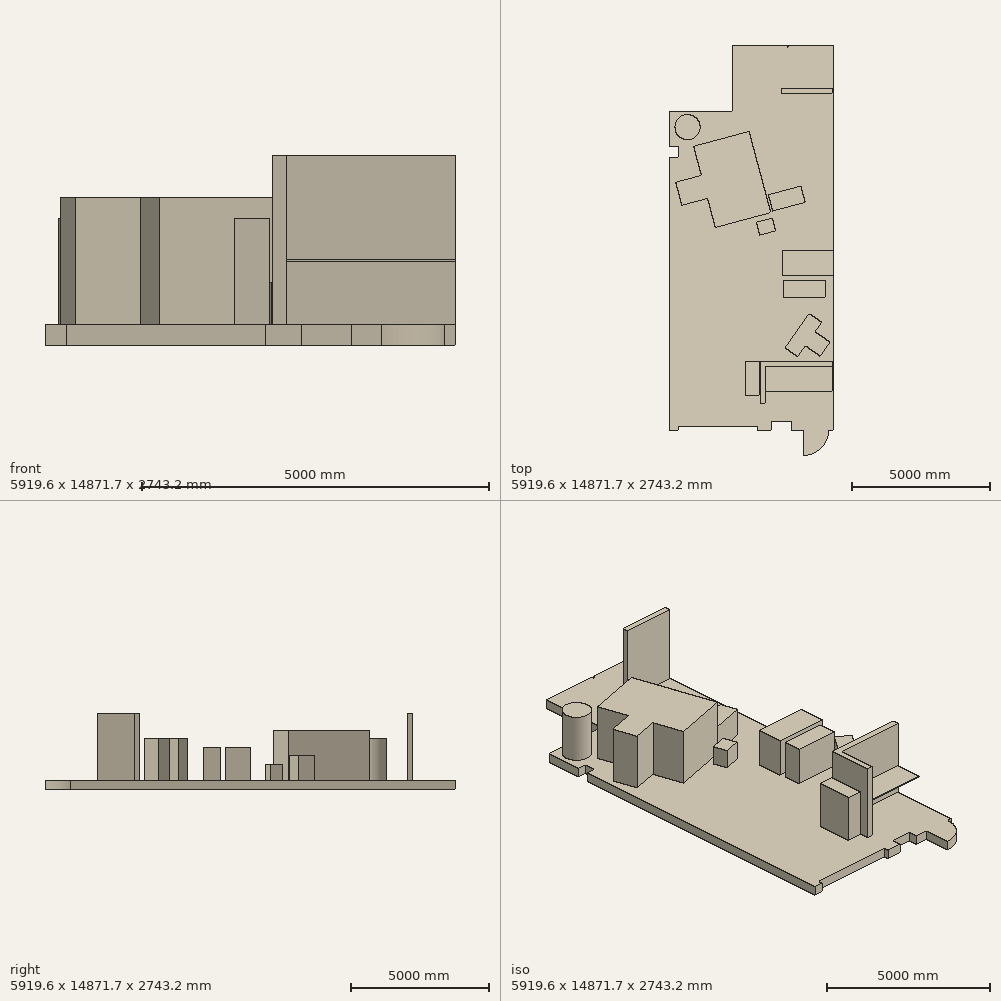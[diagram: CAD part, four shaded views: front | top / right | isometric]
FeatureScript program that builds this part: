
annotation { "Feature Type Name" : "Feature", "Feature Type Description" : "" }
export const myFeature = defineFeature(function(context is Context, id is Id, definition is map)
    precondition{}
    {
        {
            var Q0;
            Q0=qCreatedBy(makeId("Top.planeOp"),FACE);
            var sketch = newSketch(context, id + "F0", { "sketchPlane" : qUnion([Q0])});
            skLineSegment(sketch, "E0.bottom", {"start": v(-758.75, 6768.86) * mm, "end": v(2873.45, 6768.86) * mm});
            skLineSegment(sketch, "E0.top", {"start": v(-3044.75, -7188.44) * mm, "end": v(-2739.95, -7188.44) * mm});
            skLineSegment(sketch, "E0.left", {"start": v(-3044.75, 4368.56) * mm, "end": v(-3044.75, -7188.44) * mm});
            skLineSegment(sketch, "E0.right", {"start": v(2873.45, 6768.86) * mm, "end": v(2873.45, -7188.44) * mm});
            skPoint(sketch, "E0.middle", {"position": v(-85.65, -209.8) * mm});
            skLineSegment(sketch, "E1", {"start": v(-3044.75, 4368.56) * mm, "end": v(-758.75, 4368.56) * mm});
            skLineSegment(sketch, "E2", {"start": v(-758.75, 6768.86) * mm, "end": v(-758.75, 4368.56) * mm});
            skPoint(sketch, "E3.orphan", {"position": v(-3044.75, 6768.86) * mm});
            skLineSegment(sketch, "E4.top", {"start": v(-2739.95, -7036.04) * mm, "end": v(130.25, -7036.04) * mm});
            skLineSegment(sketch, "E4.left", {"start": v(-2739.95, -7188.44) * mm, "end": v(-2739.95, -7036.04) * mm});
            skLineSegment(sketch, "E4.right", {"start": v(130.25, -7188.44) * mm, "end": v(130.25, -7036.04) * mm});
            skLineSegment(sketch, "E5", {"start": v(1806.65, -7188.44) * mm, "end": v(1806.65, -8102.84) * mm});
            skPoint(sketch, "E6", {"position": v(2721.05, -7188.44) * mm});
            skArc(sketch, "E7", {"start": v(2721.05, -7188.44) * mm, "mid": v(2453.23, -7835.02) * mm, "end": v(1806.65, -8102.84) * mm});
            skLineSegment(sketch, "E8.trimOffspring", {"start": v(2721.05, -7188.44) * mm, "end": v(2873.45, -7188.44) * mm});
            skLineSegment(sketch, "E9.trimOffspring", {"start": v(130.25, -7188.44) * mm, "end": v(1806.65, -7188.44) * mm});
            skLineSegment(sketch, "E10.bottom", {"start": v(650.95, -7188.44) * mm, "end": v(1374.85, -7188.44) * mm});
            skLineSegment(sketch, "E10.top", {"start": v(650.95, -6883.64) * mm, "end": v(1374.85, -6883.64) * mm});
            skLineSegment(sketch, "E10.left", {"start": v(650.95, -7188.44) * mm, "end": v(650.95, -6883.64) * mm});
            skLineSegment(sketch, "E10.right", {"start": v(1374.85, -7188.44) * mm, "end": v(1374.85, -6883.64) * mm});
            skLineSegment(sketch, "E11.bottom", {"start": v(1222.45, 6768.86) * mm, "end": v(1273.25, 6768.86) * mm});
            skLineSegment(sketch, "E11.top", {"start": v(1222.45, 6679.15) * mm, "end": v(1273.25, 6679.15) * mm});
            skLineSegment(sketch, "E11.left", {"start": v(1273.25, 6768.86) * mm, "end": v(1273.25, 6679.15) * mm});
            skLineSegment(sketch, "E11.right", {"start": v(1222.45, 6768.86) * mm, "end": v(1222.45, 6679.15) * mm});
            skLineSegment(sketch, "E12.bottom", {"start": v(-3044.75, 3098.56) * mm, "end": v(-2739.95, 3098.56) * mm});
            skLineSegment(sketch, "E12.top", {"start": v(-3044.75, 2704.86) * mm, "end": v(-2739.95, 2704.86) * mm});
            skLineSegment(sketch, "E12.left", {"start": v(-3044.75, 3098.56) * mm, "end": v(-3044.75, 2704.86) * mm});
            skLineSegment(sketch, "E12.right", {"start": v(-2739.95, 3098.56) * mm, "end": v(-2739.95, 2704.86) * mm});
            skSolve(sketch);
        }
        {
            var Q0;
            Q0=qCreatedBy(makeId("Top.planeOp"),FACE);
            var sketch = newSketch(context, id + "F1", { "sketchPlane" : qUnion([Q0])});
            skPoint(sketch, "E13", {"position": v(-269.7, 6243.01) * mm});
            skCircle(sketch, "E14", {"center": v(-269.7, 6243.01) * mm, "radius": 457.2 * mm});
            skLineSegment(sketch, "E15.bottom", {"start": v(-2184.07, 3463.75) * mm, "end": v(-172.24, 4002.82) * mm});
            skLineSegment(sketch, "E15.top", {"start": v(-1395.19, 519.6) * mm, "end": v(616.64, 1058.68) * mm});
            skLineSegment(sketch, "E15.left", {"start": v(-2833.7, 2158.95) * mm, "end": v(-2610.18, 1324.78) * mm});
            skLineSegment(sketch, "E15.right", {"start": v(-172.24, 4002.82) * mm, "end": v(616.64, 1058.68) * mm});
            skPoint(sketch, "E15.middle", {"position": v(-777.7, 2217.11) * mm});
            skLineSegment(sketch, "E16.bottom", {"start": v(669.24, 862.4) * mm, "end": v(89.62, 707.1) * mm});
            skLineSegment(sketch, "E16.top", {"start": v(794.14, 396.25) * mm, "end": v(214.53, 240.94) * mm});
            skLineSegment(sketch, "E16.left", {"start": v(669.24, 862.4) * mm, "end": v(794.14, 396.25) * mm});
            skLineSegment(sketch, "E16.right", {"start": v(89.62, 707.1) * mm, "end": v(214.53, 240.94) * mm});
            skLineSegment(sketch, "E17.bottom", {"start": v(2549.7, 6752.11) * mm, "end": v(2041.7, 6752.11) * mm});
            skLineSegment(sketch, "E17.top", {"start": v(2549.7, 6142.51) * mm, "end": v(2041.7, 6142.51) * mm});
            skLineSegment(sketch, "E17.left", {"start": v(2549.7, 6752.11) * mm, "end": v(2549.7, 6142.51) * mm});
            skLineSegment(sketch, "E17.right", {"start": v(2041.7, 6752.11) * mm, "end": v(2041.7, 6142.51) * mm});
            skLineSegment(sketch, "E18.bottom", {"start": v(924.1, 6752.11) * mm, "end": v(1533.7, 6752.11) * mm});
            skLineSegment(sketch, "E18.top", {"start": v(924.1, 6330.69) * mm, "end": v(1533.7, 6330.69) * mm});
            skLineSegment(sketch, "E18.left", {"start": v(924.1, 6752.11) * mm, "end": v(924.1, 6330.69) * mm});
            skLineSegment(sketch, "E18.right", {"start": v(1533.7, 6752.11) * mm, "end": v(1533.7, 6330.69) * mm});
            skLineSegment(sketch, "E19.bottom", {"start": v(2846.22, 5215.41) * mm, "end": v(1017.42, 5215.41) * mm});
            skLineSegment(sketch, "E19.top", {"start": v(2846.22, 5012.21) * mm, "end": v(1017.42, 5012.21) * mm});
            skLineSegment(sketch, "E19.left", {"start": v(2846.22, 5215.41) * mm, "end": v(2846.22, 5012.21) * mm});
            skLineSegment(sketch, "E19.right", {"start": v(1017.42, 5215.41) * mm, "end": v(1017.42, 5012.21) * mm});
            skLineSegment(sketch, "E20.bottom", {"start": v(527.51, 1655.28) * mm, "end": v(1705.17, 1970.83) * mm});
            skLineSegment(sketch, "E20.top", {"start": v(685.29, 1066.45) * mm, "end": v(1862.94, 1382) * mm});
            skLineSegment(sketch, "E20.left", {"start": v(527.51, 1655.28) * mm, "end": v(685.29, 1066.45) * mm});
            skLineSegment(sketch, "E20.right", {"start": v(1705.17, 1970.83) * mm, "end": v(1862.94, 1382) * mm});
            skLineSegment(sketch, "E21.bottom", {"start": v(228.15, -6200.2) * mm, "end": v(431.35, -6200.2) * mm});
            skLineSegment(sketch, "E21.top", {"start": v(228.15, -4676.2) * mm, "end": v(431.35, -4676.2) * mm});
            skLineSegment(sketch, "E21.left", {"start": v(228.15, -6200.2) * mm, "end": v(228.15, -4676.2) * mm});
            skLineSegment(sketch, "E21.right", {"start": v(431.35, -6200.2) * mm, "end": v(431.35, -4879.4) * mm});
            skLineSegment(sketch, "E22", {"start": v(431.35, -4676.2) * mm, "end": v(2869.75, -4676.2) * mm});
            skLineSegment(sketch, "E23", {"start": v(2869.75, -4676.2) * mm, "end": v(2869.75, -4879.4) * mm});
            skLineSegment(sketch, "E24", {"start": v(2869.75, -4879.4) * mm, "end": v(431.35, -4879.4) * mm});
            skPoint(sketch, "E25", {"position": v(1430.43, -5379.79) * mm});
            skLineSegment(sketch, "E26.bottom", {"start": v(-314.55, -5910.65) * mm, "end": v(-314.55, -4691.45) * mm});
            skLineSegment(sketch, "E26.top", {"start": v(193.45, -5910.65) * mm, "end": v(193.45, -4691.45) * mm});
            skLineSegment(sketch, "E26.left", {"start": v(-314.55, -5910.65) * mm, "end": v(193.45, -5910.65) * mm});
            skLineSegment(sketch, "E26.right", {"start": v(-314.55, -4691.45) * mm, "end": v(193.45, -4691.45) * mm});
            skPoint(sketch, "E26.middle", {"position": v(1090.07, -4417.13) * mm});
            skLineSegment(sketch, "E27.bottom", {"start": v(2874.83, -1686.87) * mm, "end": v(1046.03, -1686.87) * mm});
            skLineSegment(sketch, "E27.top", {"start": v(2874.83, -772.47) * mm, "end": v(1046.03, -772.47) * mm});
            skLineSegment(sketch, "E27.left", {"start": v(2874.83, -1686.87) * mm, "end": v(2874.83, -772.47) * mm});
            skLineSegment(sketch, "E27.right", {"start": v(1046.03, -1686.87) * mm, "end": v(1046.03, -772.47) * mm});
            skPoint(sketch, "E27.middle", {"position": v(-1844.5, -983.29) * mm});
            skLineSegment(sketch, "E28.bottom", {"start": v(-432.25, -2672.14) * mm, "end": v(177.35, -2672.14) * mm});
            skLineSegment(sketch, "E28.top", {"start": v(-432.25, -4196.14) * mm, "end": v(177.35, -4196.14) * mm});
            skLineSegment(sketch, "E28.left", {"start": v(-432.25, -2672.14) * mm, "end": v(-432.25, -4196.14) * mm});
            skLineSegment(sketch, "E28.right", {"start": v(177.35, -2672.14) * mm, "end": v(177.35, -4196.14) * mm});
            skPoint(sketch, "E28.middle", {"position": v(-2606.5, -2479.1) * mm});
            skLineSegment(sketch, "E29.bottom", {"start": v(2012.55, -2954.44) * mm, "end": v(2469.79, -3274.6) * mm});
            skLineSegment(sketch, "E29.top", {"start": v(1138.42, -4202.83) * mm, "end": v(1595.66, -4523) * mm});
            skLineSegment(sketch, "E29.left", {"start": v(2012.55, -2954.44) * mm, "end": v(1138.42, -4202.83) * mm});
            skLineSegment(sketch, "E29.right", {"start": v(2770.78, -3997.2) * mm, "end": v(2414.24, -4506.38) * mm});
            skPoint(sketch, "E29.middle", {"position": v(-168.1, -2475.87) * mm});
            skLineSegment(sketch, "E30", {"start": v(-2833.7, 2158.95) * mm, "end": v(-1901.38, 2408.77) * mm});
            skLineSegment(sketch, "E31", {"start": v(-2610.18, 1324.78) * mm, "end": v(-1677.87, 1574.6) * mm});
            skLineSegment(sketch, "E32", {"start": v(-2184.07, 3463.75) * mm, "end": v(-1901.38, 2408.77) * mm});
            skLineSegment(sketch, "E33", {"start": v(-1395.19, 519.6) * mm, "end": v(-1677.87, 1574.6) * mm});
            skPoint(sketch, "E34.orphan", {"position": v(-2301.7, 3741.11) * mm});
            skPoint(sketch, "E35.orphan", {"position": v(-2301.7, 693.11) * mm});
            skLineSegment(sketch, "E36.0", {"start": v(669.24, 862.4) * mm, "end": v(616.64, 1058.68) * mm, "construction": true});
            skLineSegment(sketch, "E37", {"start": v(2770.78, -3997.2) * mm, "end": v(2229.3, -3618.05) * mm});
            skLineSegment(sketch, "E38", {"start": v(2229.3, -3618.05) * mm, "end": v(2469.79, -3274.6) * mm});
            skLineSegment(sketch, "E39", {"start": v(2414.24, -4506.38) * mm, "end": v(1872.77, -4127.24) * mm});
            skLineSegment(sketch, "E40", {"start": v(1872.77, -4127.24) * mm, "end": v(1595.66, -4523) * mm});
            skPoint(sketch, "E41.orphan", {"position": v(441.5, -1713.87) * mm});
            skPoint(sketch, "E42.orphan", {"position": v(441.5, -3237.87) * mm});
            skLineSegment(sketch, "E43.0", {"start": v(1872.77, -4127.24) * mm, "end": v(2229.3, -3618.05) * mm, "construction": true});
            skSolve(sketch);
        }
        {
            var Q0;
            Q0=makeQuery(id+"F1.imprint","IMPRINT",FACE,{"disambiguationData":[TD([[makeQuery(id+"F1.imprint","IMPRINT",EDGE,{"derivedFrom":sQuery(id+"F1.wireOp",EDGE,"E15.bottom")}),-1.0]])]});
            extrude(context, id + "F2", {"entities" : qUnion([Q0]), "depth" : 1828.8 * mm});
        }
        {
            var Q0;
            Q0=makeQuery(id+"F1.imprint","IMPRINT",FACE,{"disambiguationData":[TD([[makeQuery(id+"F1.imprint","IMPRINT",EDGE,{"derivedFrom":sQuery(id+"F1.wireOp",EDGE,"E20.bottom")}),-1.0]])]});
            extrude(context, id + "F3", {"entities" : qUnion([Q0]), "depth" : 914.4 * mm});
        }
        {
            var Q0;
            Q0=makeQuery(id+"F1.imprint","IMPRINT",FACE,{"disambiguationData":[TD([[makeQuery(id+"F1.imprint","IMPRINT",EDGE,{"derivedFrom":sQuery(id+"F1.wireOp",EDGE,"E16.bottom")}),1.0]])]});
            extrude(context, id + "F4", {"entities" : qUnion([Q0]), "depth" : 609.6 * mm});
        }
        {
            var Q0;
            Q0=makeQuery(id+"F1.imprint","IMPRINT",FACE,{"disambiguationData":[TD([[makeQuery(id+"F1.imprint","IMPRINT",EDGE,{"derivedFrom":sQuery(id+"F1.wireOp",EDGE,"E27.bottom")}),-1.0]])]});
            extrude(context, id + "F5", {"entities" : qUnion([Q0]), "depth" : 1219.2 * mm});
        }
        {
            var Q0;
            Q0=makeQuery(id+"F1.imprint","IMPRINT",FACE,{"disambiguationData":[TD([[makeQuery(id+"F1.imprint","IMPRINT",EDGE,{"derivedFrom":sQuery(id+"F1.wireOp",EDGE,"E28.bottom")}),-1.0]])]});
            extrude(context, id + "F6", {"entities" : qUnion([Q0]), "depth" : 1219.2 * mm});
        }
        {
            var Q0;
            Q0=makeQuery(id+"F1.imprint","IMPRINT",FACE,{"disambiguationData":[TD([[makeQuery(id+"F1.imprint","IMPRINT",EDGE,{"derivedFrom":sQuery(id+"F1.wireOp",EDGE,"E29.bottom")}),-1.0]])]});
            extrude(context, id + "F7", {"entities" : qUnion([Q0]), "depth" : 1524 * mm});
        }
        {
            var Q0;
            Q0=makeQuery(id+"F1.imprint","IMPRINT",FACE,{"disambiguationData":[TD([[makeQuery(id+"F1.imprint","IMPRINT",EDGE,{"derivedFrom":sQuery(id+"F1.wireOp",EDGE,"E14")}),1.0]])]});
            var Q1;
            Q1=makeQuery(id+"F1.imprint","IMPRINT",FACE,{"disambiguationData":[TD([[makeQuery(id+"F1.imprint","IMPRINT",EDGE,{"derivedFrom":sQuery(id+"F1.wireOp",EDGE,"E26.bottom")}),-1.0]])]});
            var Q2;
            Q2=sQuery(id+"F1.wireOp",EDGE,"E14");
            var Q3;
            Q3=sQuery(id+"F1.wireOp",EDGE,"E26.right");
            var Q4;
            Q4=sQuery(id+"F1.wireOp",EDGE,"E26.bottom");
            var Q5;
            Q5=sQuery(id+"F1.wireOp",EDGE,"E26.top");
            var Q6;
            Q6=sQuery(id+"F1.wireOp",EDGE,"E26.left");
            extrude(context, id + "F8", {"entities" : qUnion([Q0, Q1]), "operationType" : NewBodyOperationType.ADD, "surfaceEntities" : qUnion([Q2, Q3, Q4, Q5, Q6]), "depth" : 1524 * mm});
        }
        {
            var Q0;
            Q0=makeQuery(id+"F1.imprint","IMPRINT",FACE,{"disambiguationData":[TD([[makeQuery(id+"F1.imprint","IMPRINT",EDGE,{"derivedFrom":sQuery(id+"F1.wireOp",EDGE,"E21.bottom")}),1.0]])]});
            extrude(context, id + "F9", {"entities" : qUnion([Q0]), "depth" : 2438.4 * mm});
        }
        {
            var Q0;
            Q0=makeQuery(id+"F1.imprint","IMPRINT",FACE,{"disambiguationData":[TD([[makeQuery(id+"F1.imprint","IMPRINT",EDGE,{"derivedFrom":sQuery(id+"F1.wireOp",EDGE,"E19.bottom")}),1.0]])]});
            extrude(context, id + "F10", {"entities" : qUnion([Q0]), "depth" : 2438.4 * mm});
        }
        {
            var Q0;
            {var subQ12=sQuery(id+"F0.wireOp",EDGE,"E0.top");Q0=makeQuery(id+"F0.imprint","IMPRINT",FACE,{"disambiguationData":[TD([[makeQuery(id+"F0.imprint","IMPRINT",EDGE,{"derivedFrom":subQ12}),1.0]])]});}
            extrude(context, id + "F11", {"entities" : qUnion([Q0]), "oppositeDirection" : true, "depth" : 304.8 * mm});
        }
        {
            var Q0;
            Q0=makeQuery(id+"F9.opExtrude","SWEPT_FACE",FACE,{"disambiguationData":[OSD([sQuery(id+"F1.wireOp",EDGE,"E24")])]});
            var sketch = newSketch(context, id + "F12", { "sketchPlane" : qUnion([Q0])});
            skLineSegment(sketch, "E44.bottom", {"start": v(431.35, 914.4) * mm, "end": v(2869.75, 914.4) * mm});
            skLineSegment(sketch, "E44.top", {"start": v(431.35, 939.8) * mm, "end": v(2869.75, 939.8) * mm});
            skLineSegment(sketch, "E44.left", {"start": v(431.35, 939.8) * mm, "end": v(431.35, 914.4) * mm});
            skLineSegment(sketch, "E44.right", {"start": v(2869.75, 939.8) * mm, "end": v(2869.75, 914.4) * mm});
            skSolve(sketch);
        }
        {
            var Q0;
            Q0 = qSketchRegion(id + "F12", true);
            extrude(context, id + "F13", {"entities" : qUnion([Q0]), "operationType" : NewBodyOperationType.ADD, "depth" : 914.4 * mm});
        }
        {
            var Q0;
            Q0=makeQuery(id+"F2.opExtrude","SWEPT_BODY",BODY,{"disambiguationData":[OSD([sQuery(id+"F1.wireOp",EDGE,"E15.bottom"),sQuery(id+"F1.wireOp",EDGE,"E15.top"),sQuery(id+"F1.wireOp",EDGE,"E15.left"),sQuery(id+"F1.wireOp",EDGE,"E15.right"),sQuery(id+"F1.wireOp",EDGE,"E30"),sQuery(id+"F1.wireOp",EDGE,"E31"),sQuery(id+"F1.wireOp",EDGE,"E32"),sQuery(id+"F1.wireOp",EDGE,"E33")])]});
            transform(context, id + "F14", {"entities" : qUnion([Q0]), "transformType" : TransformType.TRANSLATION_3D, "dx" : 0 * mm, "dy" : -914.4 * mm, "dz" : 0 * mm, "makeCopy" : false});
        }
        {
            var Q0;
            Q0=makeQuery(id+"F5.opExtrude","SWEPT_BODY",BODY,{"disambiguationData":[OSD([sQuery(id+"F1.wireOp",EDGE,"E27.bottom"),sQuery(id+"F1.wireOp",EDGE,"E27.top"),sQuery(id+"F1.wireOp",EDGE,"E27.left"),sQuery(id+"F1.wireOp",EDGE,"E27.right")])]});
            transform(context, id + "F15", {"entities" : qUnion([Q0]), "transformType" : TransformType.TRANSLATION_3D, "dx" : 0 * mm, "dy" : -609.6 * mm, "dz" : 0 * mm, "makeCopy" : false});
        }
        {
            var Q0;
            Q0=makeQuery(id+"F4.opExtrude","SWEPT_BODY",BODY,{"disambiguationData":[OSD([sQuery(id+"F1.wireOp",EDGE,"E16.bottom"),sQuery(id+"F1.wireOp",EDGE,"E16.top"),sQuery(id+"F1.wireOp",EDGE,"E16.left"),sQuery(id+"F1.wireOp",EDGE,"E16.right")])]});
            transform(context, id + "F16", {"entities" : qUnion([Q0]), "transformType" : TransformType.TRANSLATION_3D, "dx" : 0 * mm, "dy" : -914.4 * mm, "dz" : 0 * mm, "makeCopy" : false});
        }
        {
            var Q0;
            Q0=makeQuery(id+"F8.opExtrude","SWEPT_BODY",BODY,{"disambiguationData":[OSD([sQuery(id+"F1.wireOp",EDGE,"E14")])]});
            transform(context, id + "F17", {"entities" : qUnion([Q0]), "transformType" : TransformType.TRANSLATION_3D, "dx" : -2133.6 * mm, "dy" : -2438.4 * mm, "dz" : 0 * mm, "makeCopy" : false});
        }
        {
            var Q0;
            Q0=makeQuery(id+"F2.opExtrude","SWEPT_BODY",BODY,{"disambiguationData":[OSD([sQuery(id+"F1.wireOp",EDGE,"E15.bottom"),sQuery(id+"F1.wireOp",EDGE,"E15.top"),sQuery(id+"F1.wireOp",EDGE,"E15.left"),sQuery(id+"F1.wireOp",EDGE,"E15.right"),sQuery(id+"F1.wireOp",EDGE,"E30"),sQuery(id+"F1.wireOp",EDGE,"E31"),sQuery(id+"F1.wireOp",EDGE,"E32"),sQuery(id+"F1.wireOp",EDGE,"E33")])]});
            var Q1;
            Q1=makeQuery(id+"F4.opExtrude","SWEPT_BODY",BODY,{"disambiguationData":[OSD([sQuery(id+"F1.wireOp",EDGE,"E16.bottom"),sQuery(id+"F1.wireOp",EDGE,"E16.top"),sQuery(id+"F1.wireOp",EDGE,"E16.left"),sQuery(id+"F1.wireOp",EDGE,"E16.right")])]});
            transform(context, id + "F18", {"entities" : qUnion([Q0, Q1]), "transformType" : TransformType.TRANSLATION_3D, "dx" : 0 * mm, "dy" : 558.8 * mm, "dz" : 0 * mm, "makeCopy" : false});
        }
        {
            var Q0;
            Q0=makeQuery(id+"F3.opExtrude","SWEPT_BODY",BODY,{"disambiguationData":[OSD([sQuery(id+"F1.wireOp",EDGE,"E20.bottom"),sQuery(id+"F1.wireOp",EDGE,"E20.top"),sQuery(id+"F1.wireOp",EDGE,"E20.left"),sQuery(id+"F1.wireOp",EDGE,"E20.right")])]});
            transform(context, id + "F19", {"entities" : qUnion([Q0]), "transformType" : TransformType.TRANSLATION_3D, "dx" : 0 * mm, "dy" : -304.8 * mm, "dz" : 0 * mm, "makeCopy" : false});
        }
        {
            var Q0;
            Q0=makeQuery(id+"F6.opExtrude","SWEPT_BODY",BODY,{"disambiguationData":[OSD([sQuery(id+"F1.wireOp",EDGE,"E28.bottom"),sQuery(id+"F1.wireOp",EDGE,"E28.top"),sQuery(id+"F1.wireOp",EDGE,"E28.left"),sQuery(id+"F1.wireOp",EDGE,"E28.right")])]});
            var Q1;
            Q1=makeQuery(id+"F6.opExtrude","SWEPT_EDGE",EDGE,{"disambiguationData":[OSD([sQuery(id+"F1.wireOp",EDGE,"E28.bottom"),sQuery(id+"F1.wireOp",EDGE,"E28.right")])]});
            transform(context, id + "F20", {"entities" : qUnion([Q0]), "transformType" : TransformType.ROTATION, "transformAxis" : qUnion([Q1]), "angle" : 90 * degree, "makeCopy" : false});
        }
        {
            var Q0;
            Q0=makeQuery(id+"F5.opExtrude","SWEPT_BODY",BODY,{"disambiguationData":[OSD([sQuery(id+"F1.wireOp",EDGE,"E27.bottom"),sQuery(id+"F1.wireOp",EDGE,"E27.top"),sQuery(id+"F1.wireOp",EDGE,"E27.left"),sQuery(id+"F1.wireOp",EDGE,"E27.right")])]});
            transform(context, id + "F21", {"entities" : qUnion([Q0]), "transformType" : TransformType.TRANSLATION_3D, "dx" : 0 * mm, "dy" : 406.4 * mm, "dz" : 0 * mm, "makeCopy" : false});
        }
        {
            var Q0;
            Q0=makeQuery(id+"F6.opExtrude","SWEPT_BODY",BODY,{"disambiguationData":[OSD([sQuery(id+"F1.wireOp",EDGE,"E28.bottom"),sQuery(id+"F1.wireOp",EDGE,"E28.top"),sQuery(id+"F1.wireOp",EDGE,"E28.left"),sQuery(id+"F1.wireOp",EDGE,"E28.right")])]});
            transform(context, id + "F22", {"entities" : qUnion([Q0]), "transformType" : TransformType.TRANSLATION_3D, "dx" : 2438.4 * mm, "dy" : 0 * mm, "dz" : 0 * mm, "makeCopy" : false});
        }
        {
            var Q0;
            Q0=makeQuery(id+"F5.opExtrude","SWEPT_BODY",BODY,{"disambiguationData":[OSD([sQuery(id+"F1.wireOp",EDGE,"E27.bottom"),sQuery(id+"F1.wireOp",EDGE,"E27.top"),sQuery(id+"F1.wireOp",EDGE,"E27.left"),sQuery(id+"F1.wireOp",EDGE,"E27.right")])]});
            var Q1;
            Q1=makeQuery(id+"F6.opExtrude","SWEPT_BODY",BODY,{"disambiguationData":[OSD([sQuery(id+"F1.wireOp",EDGE,"E28.bottom"),sQuery(id+"F1.wireOp",EDGE,"E28.top"),sQuery(id+"F1.wireOp",EDGE,"E28.left"),sQuery(id+"F1.wireOp",EDGE,"E28.right")])]});
            transform(context, id + "F23", {"entities" : qUnion([Q0, Q1]), "transformType" : TransformType.TRANSLATION_3D, "dx" : 0 * mm, "dy" : 304.8 * mm, "dz" : 0 * mm, "makeCopy" : false});
        }
    });
